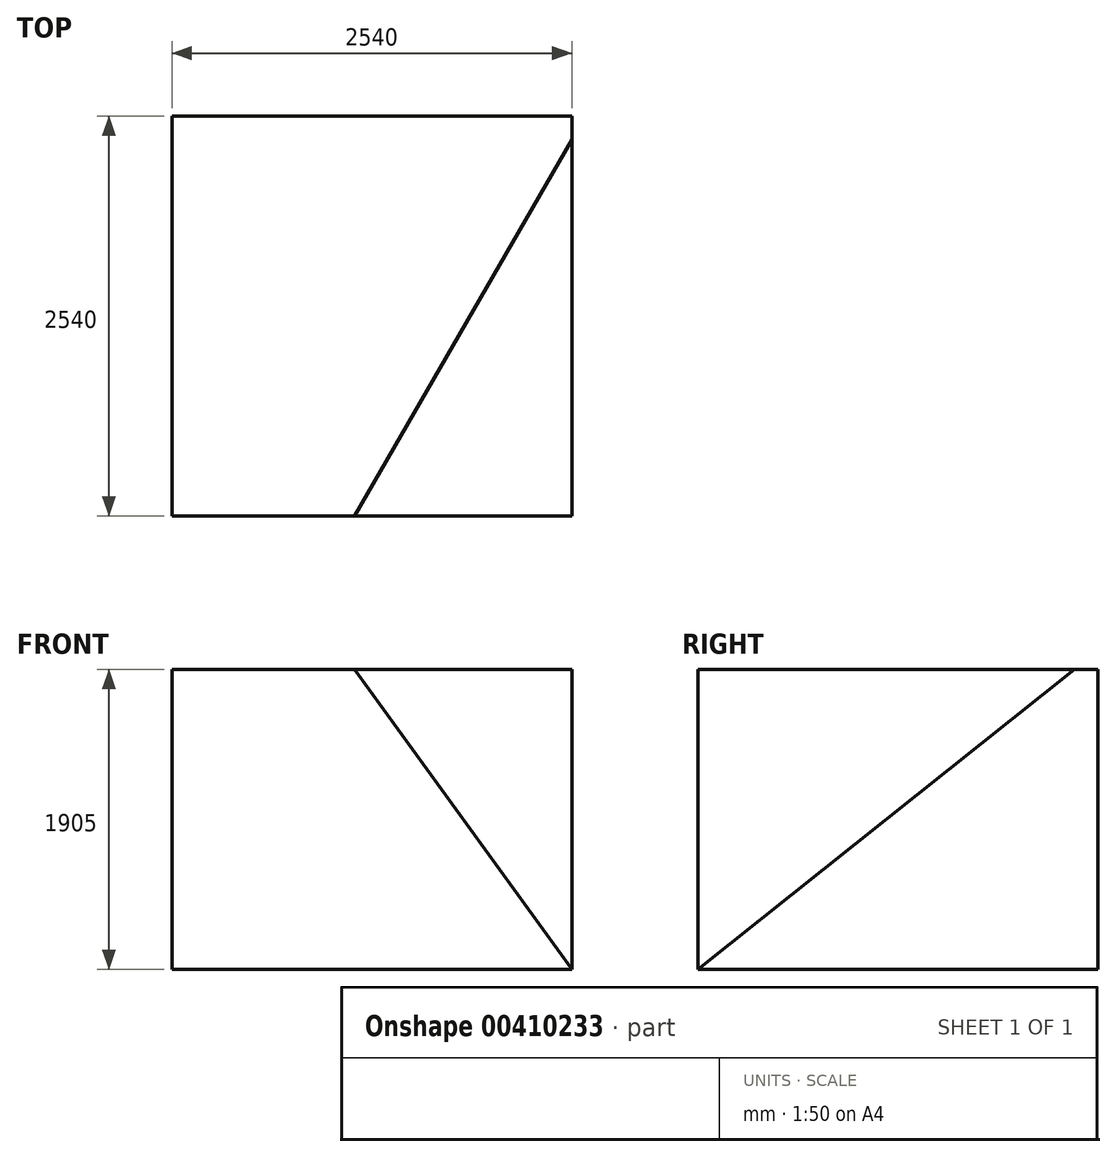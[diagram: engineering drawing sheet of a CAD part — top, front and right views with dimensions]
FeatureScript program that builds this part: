
annotation { "Feature Type Name" : "Feature", "Feature Type Description" : "" }
export const myFeature = defineFeature(function(context is Context, id is Id, definition is map)
    precondition{}
    {
        {
            var Q0;
            Q0=qCreatedBy(makeId("Top.planeOp"),FACE);
            var sketch = newSketch(context, id + "F0", { "sketchPlane" : qUnion([Q0])});
            skLineSegment(sketch, "E0.bottom", {"start": v(0, 0) * mm, "end": v(2540, 0) * mm});
            skLineSegment(sketch, "E0.top", {"start": v(0, 2540) * mm, "end": v(2540, 2540) * mm});
            skLineSegment(sketch, "E0.left", {"start": v(0, 0) * mm, "end": v(0, 2540) * mm});
            skLineSegment(sketch, "E0.right", {"start": v(2540, 0) * mm, "end": v(2540, 2540) * mm});
            skSolve(sketch);
        }
        {
            var Q0;
            Q0=makeQuery(id+"F0.imprint","IMPRINT",FACE,{"disambiguationData":[TD([[makeQuery(id+"F0.imprint","IMPRINT",EDGE,{"derivedFrom":sQuery(id+"F0.wireOp",EDGE,"E0.bottom")}),1.0]])]});
            extrude(context, id + "F1", {"entities" : qUnion([Q0]), "depth" : 1905 * mm});
        }
        {
            var Q0;
            Q0=makeQuery(id+"F1.opExtrude","CAP_FACE",FACE,{"disambiguationData":[OSD([sQuery(id+"F0.wireOp",EDGE,"E0.bottom"),sQuery(id+"F0.wireOp",EDGE,"E0.top"),sQuery(id+"F0.wireOp",EDGE,"E0.left"),sQuery(id+"F0.wireOp",EDGE,"E0.right")])],"isStart":false});
            var sketch = newSketch(context, id + "F2", { "sketchPlane" : qUnion([Q0])});
            skCircle(sketch, "E1.cCircle", {"center": v(1270, 1270) * mm, "radius": 539.37 * mm, "construction": true});
            skPoint(sketch, "E1.cCircle.centerSnap0", {"position": v(0, 1270) * mm});
            skPoint(sketch, "E1.cCircle.centerSnap1", {"position": v(1270, 2540) * mm});
            skLineSegment(sketch, "E1.0", {"start": v(958.6, 1809.37) * mm, "end": v(1581.4, 1809.37) * mm});
            skLineSegment(sketch, "E1.1", {"start": v(1581.4, 1809.37) * mm, "end": v(1892.81, 1270) * mm});
            skLineSegment(sketch, "E1.2", {"start": v(1892.81, 1270) * mm, "end": v(1581.4, 730.63) * mm});
            skLineSegment(sketch, "E1.3", {"start": v(1581.4, 730.63) * mm, "end": v(958.6, 730.63) * mm});
            skLineSegment(sketch, "E1.4", {"start": v(958.6, 730.63) * mm, "end": v(647.19, 1270) * mm});
            skLineSegment(sketch, "E1.5", {"start": v(647.19, 1270) * mm, "end": v(958.6, 1809.37) * mm});
            skPoint(sketch, "E1.0.midPoint", {"position": v(1270, 1809.37) * mm});
            skSolve(sketch);
        }
        {
            var Q0;
            Q0=makeQuery(id+"F1.opExtrude","CAP_VERTEX",VERTEX,{"disambiguationData":[OSD([sQuery(id+"F0.wireOp",EDGE,"E0.bottom"),sQuery(id+"F0.wireOp",EDGE,"E0.right")])],"isStart":true});
            var Q1;
            Q1=sQuery(id+"F2.wireOp",VERTEX,"E1.3.start");
            var Q2;
            Q2=sQuery(id+"F2.wireOp",VERTEX,"E1.2.start");
            cPlane(context, id + "F3", {"entities" : qUnion([Q0, Q1, Q2]), "cplaneType" : CPlaneType.THREE_POINT, "offset" : 25.4 * mm, "width" : 152.4 * mm, "height" : 152.4 * mm});
        }
        {
            var Q0;
            Q0=qCreatedBy(id+"F3.planeOp",FACE);
            var sketch = newSketch(context, id + "F4", { "sketchPlane" : qUnion([Q0])});
            skLineSegment(sketch, "E2", {"start": v(871.07, -1490.4) * mm, "end": v(871.07, 862.17) * mm});
            skLineSegment(sketch, "E3", {"start": v(1677.6, 614.65) * mm, "end": v(871.07, 862.17) * mm});
            skLineSegment(sketch, "E4", {"start": v(2273, 431.93) * mm, "end": v(1677.6, 614.65) * mm});
            skLineSegment(sketch, "E5", {"start": v(3510.42, 52.18) * mm, "end": v(2273, 431.93) * mm});
            skLineSegment(sketch, "E6", {"start": v(3510.42, 52.18) * mm, "end": v(871.07, -1490.4) * mm});
            skSolve(sketch);
        }
        {
            var Q0;
            Q0=makeQuery(id+"F4.imprint","IMPRINT",FACE,{"disambiguationData":[TD([[makeQuery(id+"F4.imprint","IMPRINT",EDGE,{"derivedFrom":sQuery(id+"F4.wireOp",EDGE,"E2")}),-1.0]])]});
            extrude(context, id + "F5", {"entities" : qUnion([Q0]), "operationType" : NewBodyOperationType.REMOVE, "endBound" : BoundingType.THROUGH_ALL, "depth" : 25.4 * mm});
        }
    });
